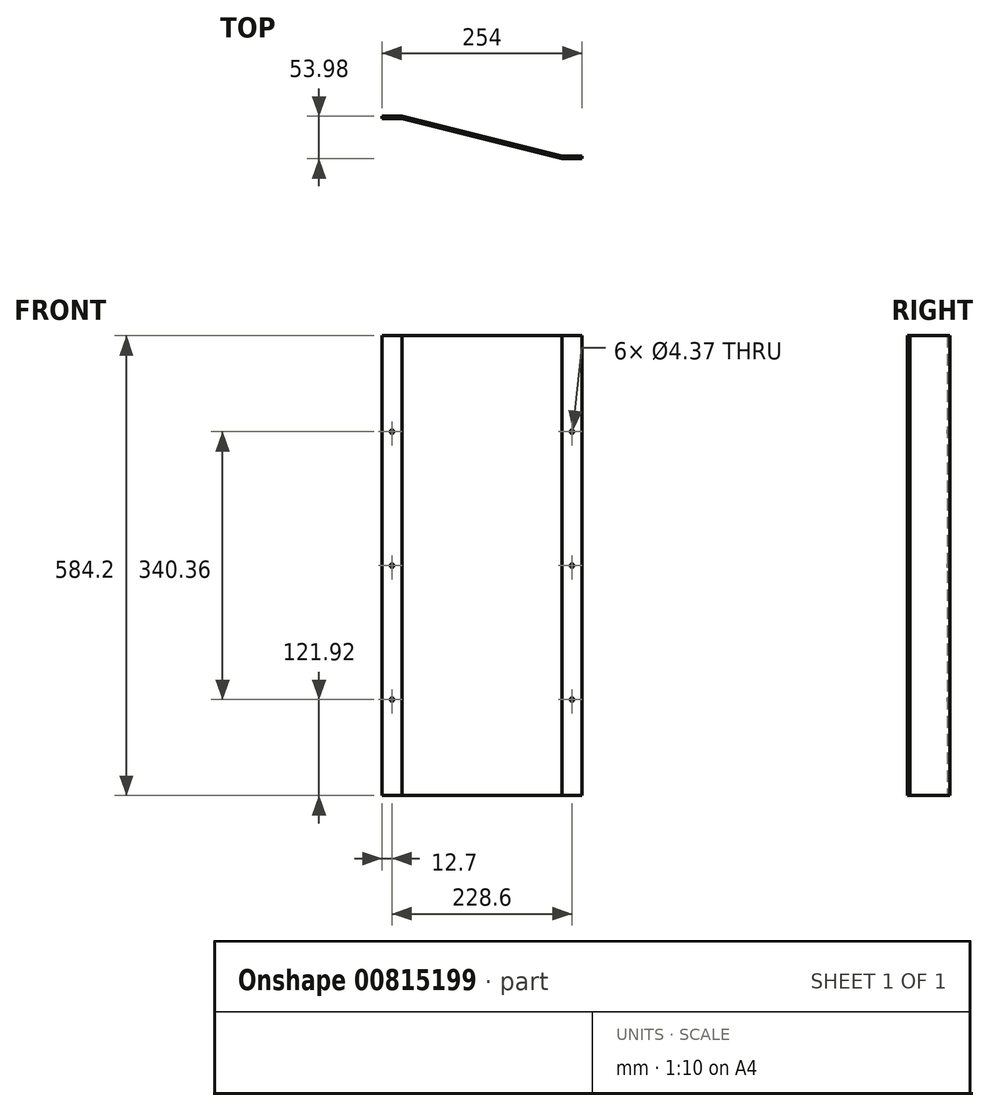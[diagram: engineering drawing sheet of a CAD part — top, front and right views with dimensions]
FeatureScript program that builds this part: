
annotation { "Feature Type Name" : "Feature", "Feature Type Description" : "" }
export const myFeature = defineFeature(function(context is Context, id is Id, definition is map)
    precondition{}
    {
        {
            var Q0;
            Q0=qCreatedBy(makeId("Top.planeOp"),FACE);
            var sketch = newSketch(context, id + "F0", { "sketchPlane" : qUnion([Q0])});
            skLineSegment(sketch, "E0.bottom", {"start": v(0, 0) * mm, "end": v(25.4, 0) * mm});
            skLineSegment(sketch, "E0.top", {"start": v(0, -3.18) * mm, "end": v(25.4, -3.18) * mm});
            skLineSegment(sketch, "E0.left", {"start": v(0, 0) * mm, "end": v(0, -3.18) * mm});
            skLineSegment(sketch, "E0.right", {"start": v(25.4, 0) * mm, "end": v(25.4, -3.18) * mm});
            skLineSegment(sketch, "E1", {"start": v(25.4, -3.17) * mm, "end": v(228.6, -53.97) * mm});
            skLineSegment(sketch, "E2.bottom", {"start": v(0, -46.77) * mm, "end": v(381, -46.77) * mm});
            skLineSegment(sketch, "E2.top", {"start": v(0, -45.5) * mm, "end": v(381, -45.5) * mm});
            skLineSegment(sketch, "E2.left", {"start": v(0, -46.77) * mm, "end": v(0, -45.5) * mm});
            skLineSegment(sketch, "E2.right", {"start": v(381, -46.77) * mm, "end": v(381, -45.5) * mm});
            skLineSegment(sketch, "E3.bottom", {"start": v(25.4, 0) * mm, "end": v(0, 0) * mm});
            skLineSegment(sketch, "E3.top", {"start": v(25.4, 25.4) * mm, "end": v(0, 25.4) * mm});
            skLineSegment(sketch, "E3.left", {"start": v(25.4, 0) * mm, "end": v(25.4, 25.4) * mm});
            skLineSegment(sketch, "E3.right", {"start": v(0, 0) * mm, "end": v(0, 25.4) * mm});
            skLineSegment(sketch, "E4.top", {"start": v(228.6, -50.8) * mm, "end": v(228.6, -50.8) * mm});
            skLineSegment(sketch, "E5.bottom", {"start": v(228.6, -50.8) * mm, "end": v(254, -50.8) * mm});
            skLineSegment(sketch, "E5.top", {"start": v(228.6, -53.97) * mm, "end": v(254, -53.97) * mm});
            skLineSegment(sketch, "E5.left", {"start": v(228.6, -50.8) * mm, "end": v(228.6, -53.97) * mm});
            skLineSegment(sketch, "E5.right", {"start": v(254, -50.8) * mm, "end": v(254, -53.97) * mm});
            skLineSegment(sketch, "E6", {"start": v(25.4, 0) * mm, "end": v(228.6, -50.8) * mm});
            skSolve(sketch);
        }
        {
            var Q0;
            Q0=makeQuery(id+"F0.imprint","IMPRINT",FACE,{"disambiguationData":[TD([[makeQuery(id+"F0.imprint","IMPRINT",EDGE,{"derivedFrom":sQuery(id+"F0.wireOp",EDGE,"E0.top")}),1.0]])]});
            var Q1;
            Q1=makeQuery(id+"F0.imprint","IMPRINT",FACE,{"disambiguationData":[TD([[makeQuery(id+"F0.imprint","IMPRINT",EDGE,{"derivedFrom":sQuery(id+"F0.wireOp",EDGE,"E0.right")}),1.0]])]});
            var Q2;
            Q2=makeQuery(id+"F0.imprint","IMPRINT",FACE,{"disambiguationData":[TD([[makeQuery(id+"F0.imprint","IMPRINT",EDGE,{"derivedFrom":sQuery(id+"F0.wireOp",EDGE,"E5.bottom")}),-1.0]])]});
            var Q3;
            {var subQ0=sQuery(id+"F0.wireOp",EDGE,"E5.left");Q3=makeQuery(id+"F0.imprint","IMPRINT",FACE,{"disambiguationData":[TD([[makeQuery(id+"F0.imprint","IMPRINT",EDGE,{"derivedFrom":subQ0}),-1.0]])]});}
            var Q4;
            {var subQ0=sQuery(id+"F0.wireOp",EDGE,"E2.top");var subQ1=sQuery(id+"F0.wireOp",EDGE,"E1");var subQ2=makeQuery(id+"F0.imprint","INTERSECT",VERTEX,{"derivedFrom":[subQ1,subQ0]});Q4=makeQuery(id+"F0.imprint","IMPRINT",FACE,{"disambiguationData":[TD([[makeQuery(id+"F0.imprint","IMPRINT",EDGE,{"disambiguationData":[TD([[subQ2,-1.0]])],"derivedFrom":subQ1}),1.0]])]});}
            extrude(context, id + "F1", {"entities" : qUnion([Q0, Q1, Q2, Q3, Q4]), "depth" : 584.2 * mm, "offsetDistance" : 25.4 * mm});
        }
        {
            var Q0;
            Q0=makeQuery(id+"F1.opExtrude","SWEPT_FACE",FACE,{"disambiguationData":[OSD([sQuery(id+"F0.wireOp",EDGE,"E0.top")])]});
            var sketch = newSketch(context, id + "F2", { "sketchPlane" : qUnion([Q0])});
            skCircle(sketch, "E7", {"center": v(12.7, 462.28) * mm, "radius": 2.18 * mm});
            skCircle(sketch, "E8", {"center": v(12.7, 292.1) * mm, "radius": 2.18 * mm});
            skCircle(sketch, "E9", {"center": v(12.7, 121.92) * mm, "radius": 2.18 * mm});
            skSolve(sketch);
        }
        {
            var Q0;
            Q0=makeQuery(id+"F2.imprint","IMPRINT",FACE,{"disambiguationData":[TD([[makeQuery(id+"F2.imprint","IMPRINT",EDGE,{"derivedFrom":sQuery(id+"F2.wireOp",EDGE,"E9")}),1.0]])]});
            var Q1;
            Q1=makeQuery(id+"F2.imprint","IMPRINT",FACE,{"disambiguationData":[TD([[makeQuery(id+"F2.imprint","IMPRINT",EDGE,{"derivedFrom":sQuery(id+"F2.wireOp",EDGE,"E8")}),1.0]])]});
            var Q2;
            Q2=makeQuery(id+"F2.imprint","IMPRINT",FACE,{"disambiguationData":[TD([[makeQuery(id+"F2.imprint","IMPRINT",EDGE,{"derivedFrom":sQuery(id+"F2.wireOp",EDGE,"E7")}),1.0]])]});
            extrude(context, id + "F3", {"entities" : qUnion([Q0, Q1, Q2]), "operationType" : NewBodyOperationType.REMOVE, "oppositeDirection" : true, "depth" : 25.4 * mm, "offsetDistance" : 25.4 * mm});
        }
        {
            var Q0;
            Q0=makeQuery(id+"F1.opExtrude","SWEPT_FACE",FACE,{"disambiguationData":[OSD([sQuery(id+"F0.wireOp",EDGE,"E5.top")])]});
            var sketch = newSketch(context, id + "F4", { "sketchPlane" : qUnion([Q0])});
            skCircle(sketch, "E10", {"center": v(241.3, 462.28) * mm, "radius": 2.18 * mm});
            skCircle(sketch, "E11", {"center": v(241.3, 121.92) * mm, "radius": 2.18 * mm});
            skCircle(sketch, "E12", {"center": v(241.3, 292.1) * mm, "radius": 2.18 * mm});
            skSolve(sketch);
        }
        {
            var Q0;
            Q0=makeQuery(id+"F4.imprint","IMPRINT",FACE,{"disambiguationData":[TD([[makeQuery(id+"F4.imprint","IMPRINT",EDGE,{"derivedFrom":sQuery(id+"F4.wireOp",EDGE,"E12")}),1.0]])]});
            var Q1;
            Q1=makeQuery(id+"F4.imprint","IMPRINT",FACE,{"disambiguationData":[TD([[makeQuery(id+"F4.imprint","IMPRINT",EDGE,{"derivedFrom":sQuery(id+"F4.wireOp",EDGE,"E10")}),1.0]])]});
            var Q2;
            Q2=makeQuery(id+"F4.imprint","IMPRINT",FACE,{"disambiguationData":[TD([[makeQuery(id+"F4.imprint","IMPRINT",EDGE,{"derivedFrom":sQuery(id+"F4.wireOp",EDGE,"E11")}),1.0]])]});
            extrude(context, id + "F5", {"entities" : qUnion([Q0, Q1, Q2]), "operationType" : NewBodyOperationType.REMOVE, "oppositeDirection" : true, "depth" : 25.4 * mm, "offsetDistance" : 25.4 * mm});
        }
    });
